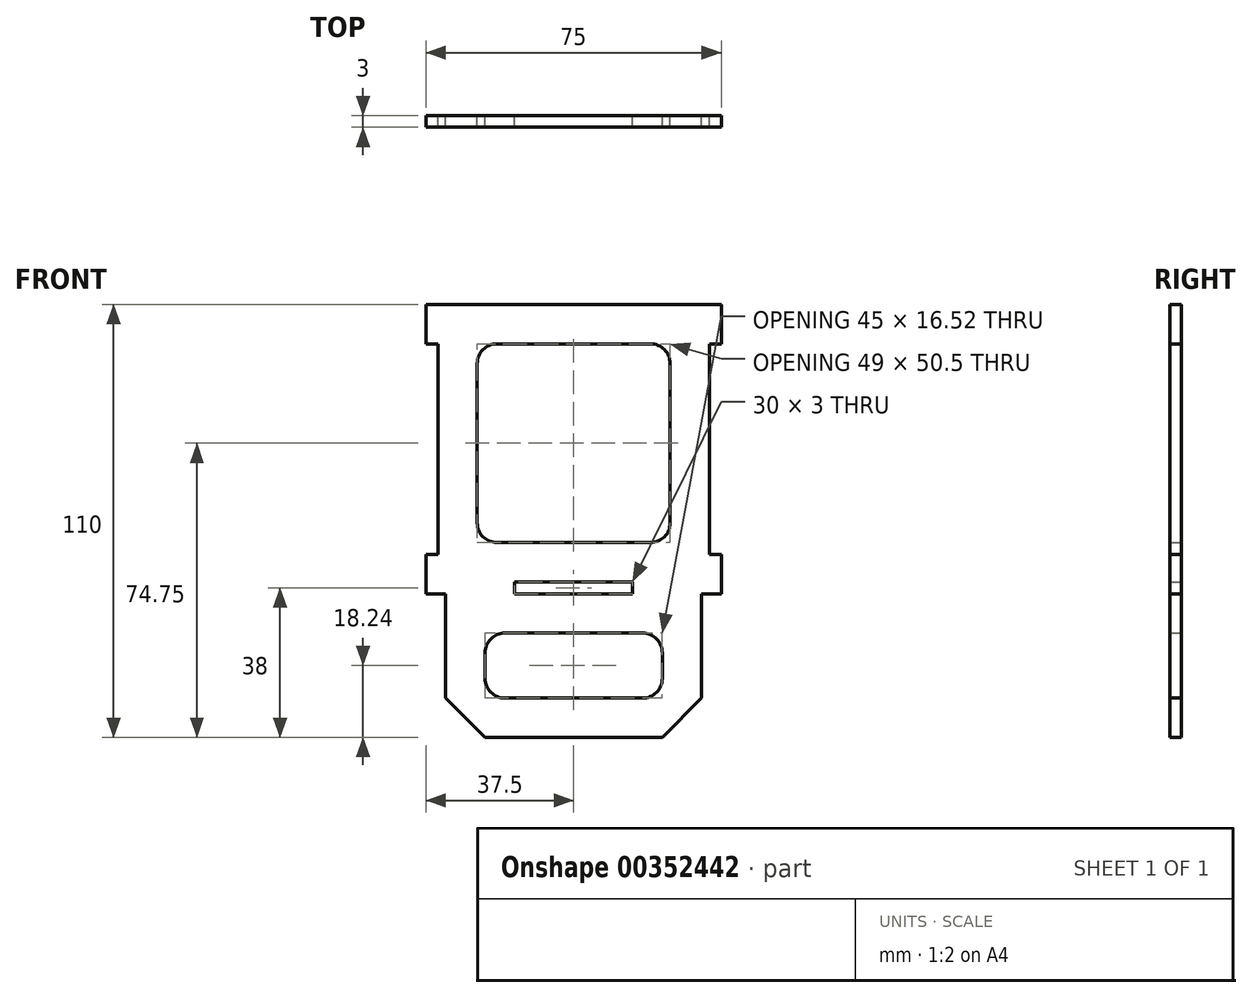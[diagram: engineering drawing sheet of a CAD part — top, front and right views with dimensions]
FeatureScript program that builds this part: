
annotation { "Feature Type Name" : "Feature", "Feature Type Description" : "" }
export const myFeature = defineFeature(function(context is Context, id is Id, definition is map)
    precondition{}
    {
        {
            var Q0;
            Q0=qCreatedBy(makeId("Front.planeOp"),FACE);
            var sketch = newSketch(context, id + "F0", { "sketchPlane" : qUnion([Q0])});
            skLineSegment(sketch, "E0.bottom", {"start": v(37.5, 55) * mm, "end": v(-37.5, 55) * mm});
            skLineSegment(sketch, "E0.top", {"start": v(22.5, -55) * mm, "end": v(-22.5, -55) * mm});
            skLineSegment(sketch, "E0.left", {"start": v(37.5, 55) * mm, "end": v(37.5, 45) * mm});
            skLineSegment(sketch, "E0.right", {"start": v(-37.5, 55) * mm, "end": v(-37.5, 45) * mm});
            skPoint(sketch, "E0.middle", {"position": v(0, 0) * mm});
            skLineSegment(sketch, "E1", {"start": v(-37.5, 45) * mm, "end": v(-34.5, 45) * mm});
            skLineSegment(sketch, "E2", {"start": v(-34.5, 45) * mm, "end": v(-34.5, -8.5) * mm});
            skLineSegment(sketch, "E3", {"start": v(-34.5, -8.5) * mm, "end": v(-37.5, -8.5) * mm});
            skLineSegment(sketch, "E4", {"start": v(37.5, 45) * mm, "end": v(34.5, 45) * mm});
            skLineSegment(sketch, "E5", {"start": v(34.5, 45) * mm, "end": v(34.5, -8.5) * mm});
            skLineSegment(sketch, "E6", {"start": v(34.5, -8.5) * mm, "end": v(37.5, -8.5) * mm});
            skLineSegment(sketch, "E7", {"start": v(-37.5, -18.5) * mm, "end": v(-32.5, -18.5) * mm});
            skLineSegment(sketch, "E8", {"start": v(-15, -15.5) * mm, "end": v(15, -15.5) * mm});
            skLineSegment(sketch, "E9", {"start": v(15, -15.5) * mm, "end": v(15, -18.5) * mm});
            skLineSegment(sketch, "E10", {"start": v(-15, -18.5) * mm, "end": v(-15, -15.5) * mm});
            skLineSegment(sketch, "E11", {"start": v(-32.5, -18.5) * mm, "end": v(-32.5, -45) * mm});
            skLineSegment(sketch, "E12", {"start": v(-32.5, -45) * mm, "end": v(-22.5, -55) * mm});
            skLineSegment(sketch, "E13", {"start": v(-15, -18.5) * mm, "end": v(15, -18.5) * mm});
            skLineSegment(sketch, "E14.trimOffspring", {"start": v(-37.5, -8.5) * mm, "end": v(-37.5, -18.5) * mm});
            skLineSegment(sketch, "E15.MirrorCS", {"start": v(32.5, -45) * mm, "end": v(22.5, -55) * mm});
            skLineSegment(sketch, "E16.MirrorCS", {"start": v(32.5, -18.5) * mm, "end": v(32.5, -45) * mm});
            skLineSegment(sketch, "E17.MirrorCS", {"start": v(37.5, -18.5) * mm, "end": v(32.5, -18.5) * mm});
            skLineSegment(sketch, "E18.trimOffspring", {"start": v(37.5, -8.5) * mm, "end": v(37.5, -18.5) * mm});
            skLineSegment(sketch, "E19.bottom", {"start": v(19.5, -5.5) * mm, "end": v(-19.5, -5.5) * mm});
            skLineSegment(sketch, "E19.top", {"start": v(19.5, 45) * mm, "end": v(-19.5, 45) * mm});
            skLineSegment(sketch, "E19.left", {"start": v(24.5, -0.5) * mm, "end": v(24.5, 40) * mm});
            skLineSegment(sketch, "E19.right", {"start": v(-24.5, -0.5) * mm, "end": v(-24.5, 40) * mm});
            skPoint(sketch, "E20.visualSharp", {"position": v(-24.5, 45) * mm});
            skArc(sketch, "E20.filletArc", {"start": v(-19.5, 45) * mm, "mid": v(-23.04, 43.54) * mm, "end": v(-24.5, 40) * mm});
            skPoint(sketch, "E21.visualSharp", {"position": v(24.5, 45) * mm});
            skArc(sketch, "E21.filletArc", {"start": v(24.5, 40) * mm, "mid": v(23.04, 43.54) * mm, "end": v(19.5, 45) * mm});
            skPoint(sketch, "E22.visualSharp", {"position": v(24.5, -5.5) * mm});
            skArc(sketch, "E22.filletArc", {"start": v(19.5, -5.5) * mm, "mid": v(23.04, -4.04) * mm, "end": v(24.5, -0.5) * mm});
            skPoint(sketch, "E23.visualSharp", {"position": v(-24.5, -5.5) * mm});
            skArc(sketch, "E23.filletArc", {"start": v(-24.5, -0.5) * mm, "mid": v(-23.04, -4.04) * mm, "end": v(-19.5, -5.5) * mm});
            skLineSegment(sketch, "E24.bottom", {"start": v(17.5, -45.02) * mm, "end": v(-17.5, -45.02) * mm});
            skLineSegment(sketch, "E24.top", {"start": v(17.5, -28.5) * mm, "end": v(-17.5, -28.5) * mm});
            skLineSegment(sketch, "E24.left", {"start": v(22.5, -40.02) * mm, "end": v(22.5, -33.5) * mm});
            skLineSegment(sketch, "E24.right", {"start": v(-22.5, -40.02) * mm, "end": v(-22.5, -33.5) * mm});
            skPoint(sketch, "E24.middle", {"position": v(0, -36.76) * mm});
            skPoint(sketch, "E25.visualSharp", {"position": v(-22.5, -28.5) * mm});
            skArc(sketch, "E25.filletArc", {"start": v(-17.5, -28.5) * mm, "mid": v(-21.04, -29.96) * mm, "end": v(-22.5, -33.5) * mm});
            skPoint(sketch, "E26.visualSharp", {"position": v(22.5, -28.5) * mm});
            skArc(sketch, "E26.filletArc", {"start": v(22.5, -33.5) * mm, "mid": v(21.04, -29.96) * mm, "end": v(17.5, -28.5) * mm});
            skPoint(sketch, "E27.visualSharp", {"position": v(22.5, -45.02) * mm});
            skArc(sketch, "E27.filletArc", {"start": v(17.5, -45.02) * mm, "mid": v(21.04, -43.56) * mm, "end": v(22.5, -40.02) * mm});
            skPoint(sketch, "E28.visualSharp", {"position": v(-22.5, -45.02) * mm});
            skArc(sketch, "E28.filletArc", {"start": v(-22.5, -40.02) * mm, "mid": v(-21.04, -43.56) * mm, "end": v(-17.5, -45.02) * mm});
            skLineSegment(sketch, "E29", {"start": v(-34.5, -8.5) * mm, "end": v(-34.5, -18.5) * mm, "construction": true});
            skLineSegment(sketch, "E30", {"start": v(34.5, -8.5) * mm, "end": v(34.5, -18.5) * mm, "construction": true});
            skSolve(sketch);
        }
        {
            var Q0;
            Q0=makeQuery(id+"F0.imprint","IMPRINT",FACE,{"disambiguationData":[TD([[makeQuery(id+"F0.imprint","IMPRINT",EDGE,{"derivedFrom":sQuery(id+"F0.wireOp",EDGE,"E0.bottom")}),1.0]])]});
            extrude(context, id + "F1", {"entities" : qUnion([Q0]), "depth" : 3 * mm, "symmetric" : true});
        }
    });
